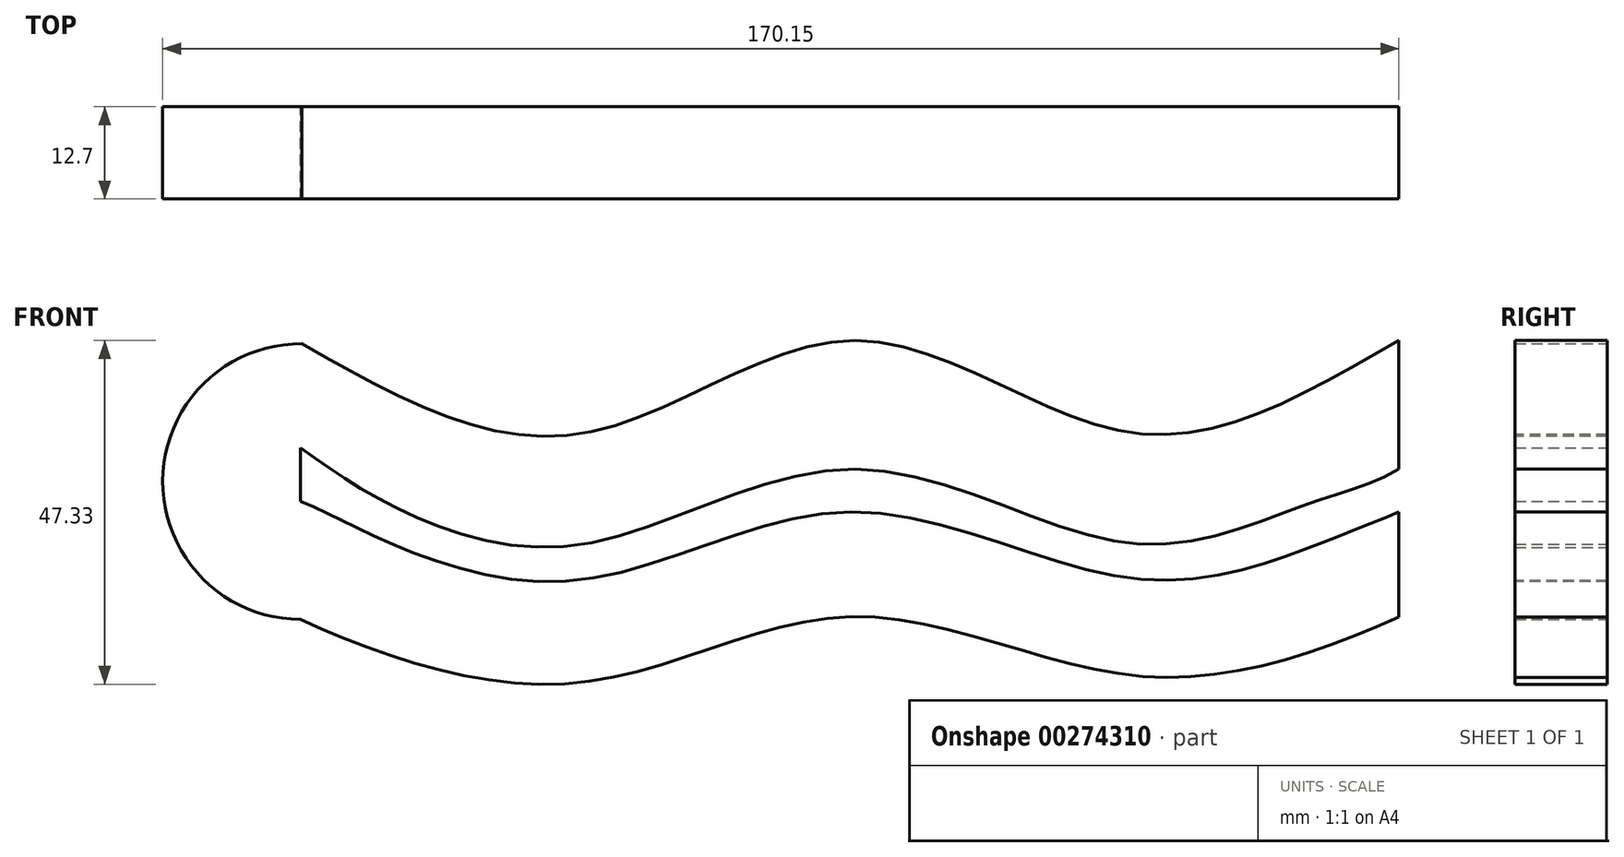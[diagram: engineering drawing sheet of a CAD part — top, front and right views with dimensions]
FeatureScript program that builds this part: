
annotation { "Feature Type Name" : "Feature", "Feature Type Description" : "" }
export const myFeature = defineFeature(function(context is Context, id is Id, definition is map)
    precondition{}
    {
        {
            var Q0;
            Q0=qCreatedBy(makeId("Front.planeOp"),FACE);
            var sketch = newSketch(context, id + "F0", { "sketchPlane" : qUnion([Q0])});
            skFitSpline(sketch, "E0", {"points": [v(-76.2, -0.44) * mm, v(-38.1, -12.89) * mm, v(0, 0) * mm, v(38.1, -12.7) * mm, v(74.8, 0) * mm], "startDerivative": vector(152.4, -87.09) * mm, "endDerivative": vector(152.4, 87.09) * mm});
            skLineSegment(sketch, "E1", {"start": v(74.8, 0) * mm, "end": v(74.8, -19.05) * mm});
            skLineSegment(sketch, "E2", {"start": v(74.8, -38.1) * mm, "end": v(74.8, -19.05) * mm});
            skLineSegment(sketch, "E3", {"start": v(-76.37, 0) * mm, "end": v(-76.37, -19.42) * mm});
            skLineSegment(sketch, "E4", {"start": v(-76.37, -19.42) * mm, "end": v(-76.37, -38.4) * mm});
            skArc(sketch, "E5", {"start": v(-76.2, -0.44) * mm, "mid": v(-95.35, -19.33) * mm, "end": v(-76.37, -38.4) * mm});
            skArc(sketch, "E6", {"start": v(74.8, 0) * mm, "mid": v(93.85, -19.05) * mm, "end": v(74.8, -38.1) * mm});
            skFitSpline(sketch, "E7", {"points": [v(-76.37, -38.4) * mm, v(-38.21, -47.12) * mm, v(-0.58, -38) * mm, v(38.6, -46.15) * mm, v(74.8, -38.1) * mm], "startDerivative": vector(130.32, -60.1) * mm, "endDerivative": vector(141.13, 62.45) * mm});
            skLineSegment(sketch, "E8", {"start": v(0, 0) * mm, "end": v(0, -17.7) * mm});
            skLineSegment(sketch, "E9", {"start": v(-0.58, -38) * mm, "end": v(-0.58, -23.6) * mm});
            skLineSegment(sketch, "E10", {"start": v(-76.37, 0) * mm, "end": v(-76.37, -14.75) * mm});
            skLineSegment(sketch, "E11", {"start": v(-76.37, -38.4) * mm, "end": v(-76.37, -22.12) * mm});
            skFitSpline(sketch, "E12", {"points": [v(-76.37, -14.75) * mm, v(-63.5, -22.86) * mm, v(-38.1, -28.13) * mm, v(0, -17.7) * mm, v(38.1, -27.94) * mm, v(62.26, -22.5) * mm, v(74.8, -17.7) * mm], "startDerivative": vector(87.73, -64.48) * mm, "endDerivative": vector(91.42, 56.37) * mm});
            skFitSpline(sketch, "E13", {"points": [v(-76.37, -22.12) * mm, v(-65.46, -27.27) * mm, v(-38.21, -33) * mm, v(-0.58, -23.6) * mm, v(38.6, -32.83) * mm, v(63.29, -28.2) * mm, v(74.8, -23.6) * mm], "startDerivative": vector(82.87, -32.67) * mm, "endDerivative": vector(89.03, 37.04) * mm});
            skSolve(sketch);
        }
        {
            var Q0;
            {var subQ1=sQuery(id+"F0.wireOp",EDGE,"E3");Q0=makeQuery(id+"F0.imprint","IMPRINT",FACE,{"disambiguationData":[TD([[makeQuery(id+"F0.imprint","IMPRINT",EDGE,{"derivedFrom":subQ1}),-1.0]])]});}
            var Q1;
            {var subQ0=sQuery(id+"F0.wireOp",EDGE,"E8");Q1=makeQuery(id+"F0.imprint","IMPRINT",FACE,{"disambiguationData":[TD([[makeQuery(id+"F0.imprint","IMPRINT",EDGE,{"derivedFrom":subQ0}),-1.0]])]});}
            var Q2;
            {var subQ2=sQuery(id+"F0.wireOp",EDGE,"E9");Q2=makeQuery(id+"F0.imprint","IMPRINT",FACE,{"disambiguationData":[TD([[makeQuery(id+"F0.imprint","IMPRINT",EDGE,{"derivedFrom":subQ2}),1.0]])]});}
            var Q3;
            {var subQ5=sQuery(id+"F0.wireOp",EDGE,"E9");Q3=makeQuery(id+"F0.imprint","IMPRINT",FACE,{"disambiguationData":[TD([[makeQuery(id+"F0.imprint","IMPRINT",EDGE,{"derivedFrom":subQ5}),-1.0]])]});}
            var Q4;
            {var subQ3=sQuery(id+"F0.wireOp",EDGE,"E8");Q4=makeQuery(id+"F0.imprint","IMPRINT",FACE,{"disambiguationData":[TD([[makeQuery(id+"F0.imprint","IMPRINT",EDGE,{"derivedFrom":subQ3}),1.0]])]});}
            var Q5;
            {var subQ4=sQuery(id+"F0.wireOp",EDGE,"E6");Q5=makeQuery(id+"F0.imprint","IMPRINT",FACE,{"disambiguationData":[TD([[makeQuery(id+"F0.imprint","IMPRINT",EDGE,{"derivedFrom":subQ4}),-1.0]])]});}
            extrude(context, id + "F1", {"entities" : qUnion([Q0, Q1, Q2, Q3, Q4, Q5]), "depth" : 12.7 * mm});
        }
    });
